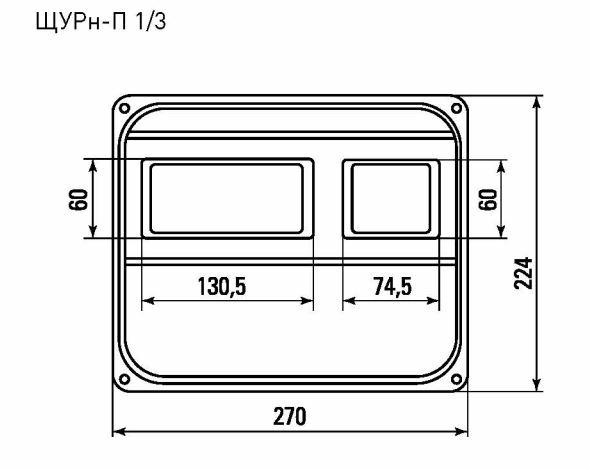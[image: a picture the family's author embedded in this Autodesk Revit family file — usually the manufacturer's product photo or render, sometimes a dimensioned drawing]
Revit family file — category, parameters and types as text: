
# Revit family: EKF_EE_Короб_КСС(1200х300х150)_Basic
name_source: partatom
category: Электрооборудование
units: mm (PartAtom-declared; Revit-internal decimal feet)

## family parameters
Всегда вертикально = Да
На основе рабочей плоскости = Нет
Общий = Нет
При загрузке вырезать с полостями = Нет
Размер круглого соединителя = Использовать диаметр
Тип детали = Силовой щит
Точка расчета площади = Да

## types (1)
- Короб КСС (1200х300х150) EKF Basic
    ADSK_Единица измерения = компл.
    ADSK_Завод-изготовитель = EKF
    ADSK_Классификация нагрузок = Прочее
    ADSK_Код изделия = uerm2-kss-1200-bas
    ADSK_Количество = 1
    ADSK_Количество фаз = 3
    ADSK_Коэффициент мощности = 1
    ADSK_Марка = Короб КСС
    ADSK_Масса = 0
    ADSK_Материал = RAL 7035_Сталь
    ADSK_Наименование = Короб КСС (1200х300х150) EKF BasicКороб КСС (1200х300х150) EKF Basic
    ADSK_Напряжение = 400 В
    ADSK_Номинальная мощность = 0 Вт
    ADSK_Обозначение = Короб КСС
    ADSK_Полная мощность = 0 В·А
    ADSK_Размер_Высота = 1200 мм
    ADSK_Размер_Глубина = 150 мм
    ADSK_Размер_Ширина = 300 мм
    ADSK_Ток = 125 А
    Изготовитель = EKF
    Количество DIN-реек = 0
    Количество модулей на DIN-рейке = 0
    Максимальное количество модулей = 0
    Описание = Короб КСС (1200х300х150) EKF BasicКороб КСС (1200х300х150) EKF Basic
    Серия номенклатуры = Basic
    Степень защиты IP = IP31
    ТВ = EKF
    Тип = 210 мм
    Тип установки = Навесной
